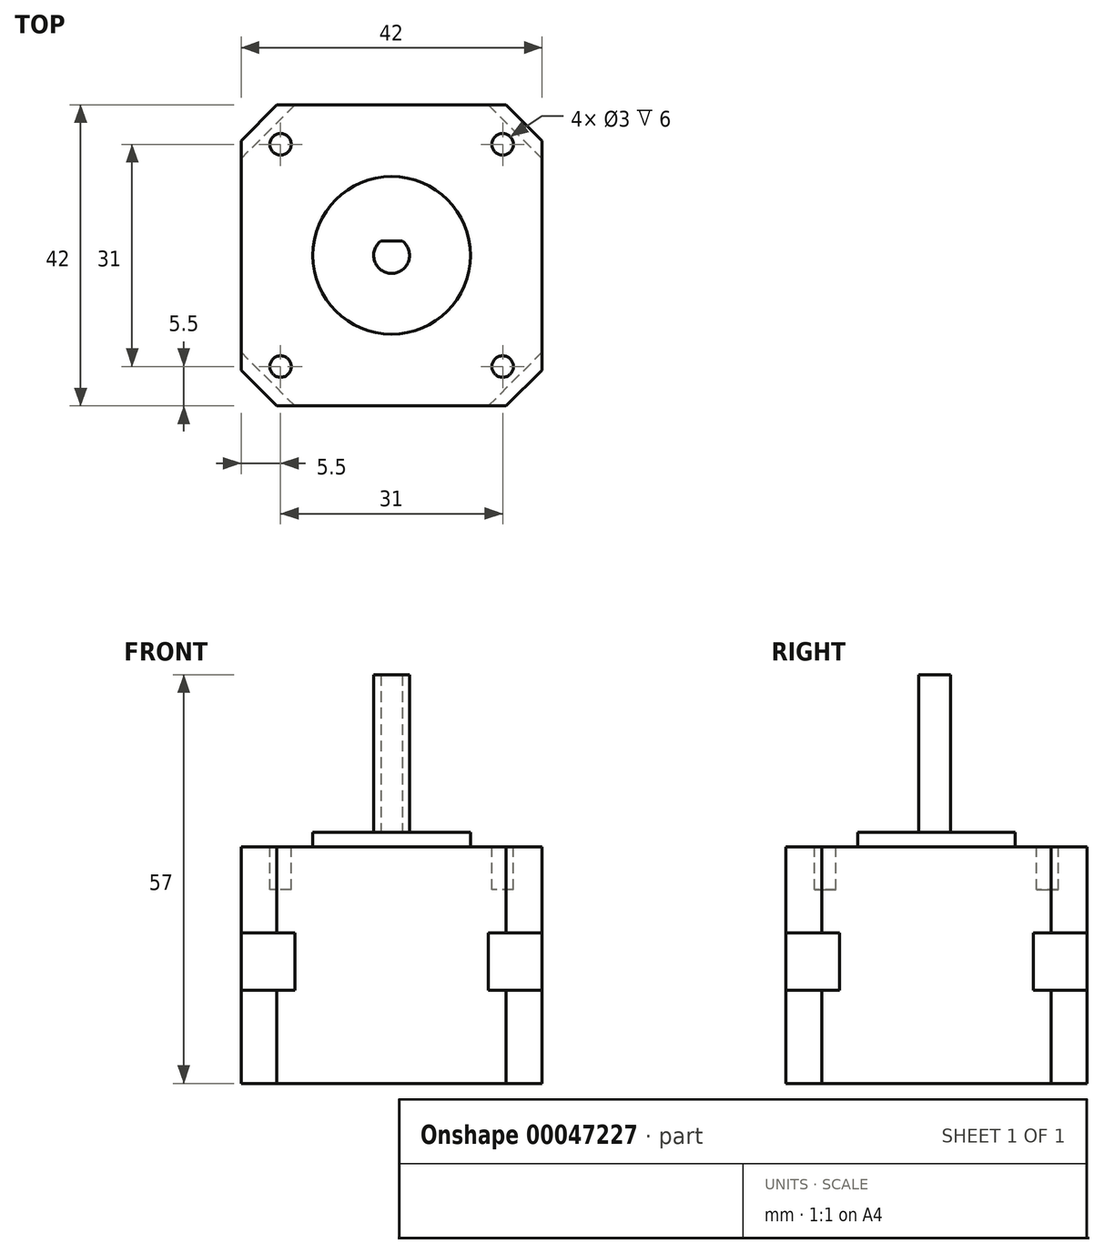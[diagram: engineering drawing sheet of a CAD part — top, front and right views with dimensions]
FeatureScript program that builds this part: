
annotation { "Feature Type Name" : "Feature", "Feature Type Description" : "" }
export const myFeature = defineFeature(function(context is Context, id is Id, definition is map)
    precondition{}
    {
        {
            var Q0;
            Q0=qCreatedBy(makeId("Top.planeOp"),FACE);
            var sketch = newSketch(context, id + "F0", { "sketchPlane" : qUnion([Q0])});
            skLineSegment(sketch, "E0.bottom", {"start": v(-21, 21) * mm, "end": v(21, 21) * mm});
            skLineSegment(sketch, "E0.top", {"start": v(-21, -21) * mm, "end": v(21, -21) * mm});
            skLineSegment(sketch, "E0.left", {"start": v(-21, 21) * mm, "end": v(-21, -21) * mm});
            skLineSegment(sketch, "E0.right", {"start": v(21, 21) * mm, "end": v(21, -21) * mm});
            skSolve(sketch);
        }
        {
            var Q0;
            Q0=makeQuery(id+"F0.imprint","IMPRINT",FACE,{"disambiguationData":[TD([[makeQuery(id+"F0.imprint","IMPRINT",EDGE,{"derivedFrom":sQuery(id+"F0.wireOp",EDGE,"E0.bottom")}),-1.0]])]});
            extrude(context, id + "F1", {"entities" : qUnion([Q0]), "endBound" : BoundingType.SYMMETRIC, "depth" : 8 * mm});
        }
        {
            var Q0;
            Q0=makeQuery(id+"F1.opExtrude","SWEPT_EDGE",EDGE,{"disambiguationData":[OSD([sQuery(id+"F0.wireOp",EDGE,"E0.bottom"),sQuery(id+"F0.wireOp",EDGE,"E0.right")])]});
            var Q1;
            Q1=makeQuery(id+"F1.opExtrude","SWEPT_EDGE",EDGE,{"disambiguationData":[OSD([sQuery(id+"F0.wireOp",EDGE,"E0.bottom"),sQuery(id+"F0.wireOp",EDGE,"E0.left")])]});
            var Q2;
            Q2=makeQuery(id+"F1.opExtrude","SWEPT_EDGE",EDGE,{"disambiguationData":[OSD([sQuery(id+"F0.wireOp",EDGE,"E0.top"),sQuery(id+"F0.wireOp",EDGE,"E0.left")])]});
            var Q3;
            Q3=makeQuery(id+"F1.opExtrude","SWEPT_EDGE",EDGE,{"disambiguationData":[OSD([sQuery(id+"F0.wireOp",EDGE,"E0.top"),sQuery(id+"F0.wireOp",EDGE,"E0.right")])]});
            chamfer(context, id + "F2", {"entities" : qUnion([Q0, Q1, Q2, Q3]), "width" : 7.5 * mm, "tangentPropagation" : true});
        }
        {
            var Q0;
            Q0=makeQuery(id+"F1.opExtrude","CAP_FACE",FACE,{"disambiguationData":[OSD([sQuery(id+"F0.wireOp",EDGE,"E0.bottom"),sQuery(id+"F0.wireOp",EDGE,"E0.top"),sQuery(id+"F0.wireOp",EDGE,"E0.left"),sQuery(id+"F0.wireOp",EDGE,"E0.right")])],"isStart":false});
            var sketch = newSketch(context, id + "F3", { "sketchPlane" : qUnion([Q0])});
            skLineSegment(sketch, "E1.0", {"start": v(-21, 21) * mm, "end": v(21, 21) * mm});
            skLineSegment(sketch, "E1.1", {"start": v(-21, 21) * mm, "end": v(-21, -21) * mm});
            skLineSegment(sketch, "E1.2", {"start": v(-21, -21) * mm, "end": v(21, -21) * mm});
            skLineSegment(sketch, "E1.3", {"start": v(21, 21) * mm, "end": v(21, -21) * mm});
            skSolve(sketch);
        }
        {
            var Q0;
            {var subQ0=sQuery(id+"F0.wireOp",EDGE,"E0.top");var subQ1=sQuery(id+"F0.wireOp",EDGE,"E0.right");var subQ2=sQuery(id+"F0.wireOp",EDGE,"E0.bottom");var subQ3=sQuery(id+"F0.wireOp",EDGE,"E0.left");var subQ4=makeQuery(id+"F1.opExtrude","CAP_FACE",FACE,{"disambiguationData":[OSD([subQ2,subQ0,subQ3,subQ1])],"isStart":false});var subQ8=makeQuery(id+"F2.opChamfer","BLEND_EDGE",EDGE,{"blendedFrom":[makeQuery(id+"F1.opExtrude","SWEPT_EDGE",EDGE,{"disambiguationData":[OSD([subQ2,subQ3])]}),subQ4],"blendedInto":[subQ4]});Q0=makeQuery(id+"F3.imprint","IMPRINT",FACE,{"disambiguationData":[TD([[makeQuery(id+"F3.imprint","IMPRINT",EDGE,{"derivedFrom":subQ8}),1.0]])]});}
            var Q1;
            {var subQ0=sQuery(id+"F0.wireOp",EDGE,"E0.bottom");var subQ1=sQuery(id+"F0.wireOp",EDGE,"E0.right");var subQ2=makeQuery(id+"F2.opChamfer","BLEND_EDGE",EDGE,{"blendedFrom":[makeQuery(id+"F1.opExtrude","SWEPT_EDGE",EDGE,{"disambiguationData":[OSD([subQ0,subQ1])]}),makeQuery(id+"F1.opExtrude","CAP_FACE",FACE,{"disambiguationData":[OSD([subQ0,sQuery(id+"F0.wireOp",EDGE,"E0.top"),sQuery(id+"F0.wireOp",EDGE,"E0.left"),subQ1])],"isStart":false})],"blendedInto":[makeQuery(id+"F1.opExtrude","CAP_FACE",FACE,{"disambiguationData":[OSD([subQ0,sQuery(id+"F0.wireOp",EDGE,"E0.top"),sQuery(id+"F0.wireOp",EDGE,"E0.left"),subQ1])],"isStart":false})]});Q1=makeQuery(id+"F3.imprint","IMPRINT",FACE,{"disambiguationData":[TD([[makeQuery(id+"F3.imprint","IMPRINT",EDGE,{"derivedFrom":subQ2}),-1.0]])]});}
            var Q2;
            {var subQ0=sQuery(id+"F0.wireOp",EDGE,"E0.bottom");var subQ1=sQuery(id+"F0.wireOp",EDGE,"E0.left");var subQ2=makeQuery(id+"F2.opChamfer","BLEND_EDGE",EDGE,{"blendedFrom":[makeQuery(id+"F1.opExtrude","SWEPT_EDGE",EDGE,{"disambiguationData":[OSD([subQ0,subQ1])]}),makeQuery(id+"F1.opExtrude","CAP_FACE",FACE,{"disambiguationData":[OSD([subQ0,sQuery(id+"F0.wireOp",EDGE,"E0.top"),subQ1,sQuery(id+"F0.wireOp",EDGE,"E0.right")])],"isStart":false})],"blendedInto":[makeQuery(id+"F1.opExtrude","CAP_FACE",FACE,{"disambiguationData":[OSD([subQ0,sQuery(id+"F0.wireOp",EDGE,"E0.top"),subQ1,sQuery(id+"F0.wireOp",EDGE,"E0.right")])],"isStart":false})]});Q2=makeQuery(id+"F3.imprint","IMPRINT",FACE,{"disambiguationData":[TD([[makeQuery(id+"F3.imprint","IMPRINT",EDGE,{"derivedFrom":subQ2}),-1.0]])]});}
            var Q3;
            {var subQ0=sQuery(id+"F0.wireOp",EDGE,"E0.top");var subQ1=sQuery(id+"F0.wireOp",EDGE,"E0.left");var subQ2=makeQuery(id+"F2.opChamfer","BLEND_EDGE",EDGE,{"blendedFrom":[makeQuery(id+"F1.opExtrude","SWEPT_EDGE",EDGE,{"disambiguationData":[OSD([subQ0,subQ1])]}),makeQuery(id+"F1.opExtrude","CAP_FACE",FACE,{"disambiguationData":[OSD([sQuery(id+"F0.wireOp",EDGE,"E0.bottom"),subQ0,subQ1,sQuery(id+"F0.wireOp",EDGE,"E0.right")])],"isStart":false})],"blendedInto":[makeQuery(id+"F1.opExtrude","CAP_FACE",FACE,{"disambiguationData":[OSD([sQuery(id+"F0.wireOp",EDGE,"E0.bottom"),subQ0,subQ1,sQuery(id+"F0.wireOp",EDGE,"E0.right")])],"isStart":false})]});Q3=makeQuery(id+"F3.imprint","IMPRINT",FACE,{"disambiguationData":[TD([[makeQuery(id+"F3.imprint","IMPRINT",EDGE,{"derivedFrom":subQ2}),-1.0]])]});}
            var Q4;
            {var subQ0=sQuery(id+"F0.wireOp",EDGE,"E0.top");var subQ1=sQuery(id+"F0.wireOp",EDGE,"E0.right");var subQ2=makeQuery(id+"F2.opChamfer","BLEND_EDGE",EDGE,{"blendedFrom":[makeQuery(id+"F1.opExtrude","SWEPT_EDGE",EDGE,{"disambiguationData":[OSD([subQ0,subQ1])]}),makeQuery(id+"F1.opExtrude","CAP_FACE",FACE,{"disambiguationData":[OSD([sQuery(id+"F0.wireOp",EDGE,"E0.bottom"),subQ0,sQuery(id+"F0.wireOp",EDGE,"E0.left"),subQ1])],"isStart":false})],"blendedInto":[makeQuery(id+"F1.opExtrude","CAP_FACE",FACE,{"disambiguationData":[OSD([sQuery(id+"F0.wireOp",EDGE,"E0.bottom"),subQ0,sQuery(id+"F0.wireOp",EDGE,"E0.left"),subQ1])],"isStart":false})]});Q4=makeQuery(id+"F3.imprint","IMPRINT",FACE,{"disambiguationData":[TD([[makeQuery(id+"F3.imprint","IMPRINT",EDGE,{"derivedFrom":subQ2}),-1.0]])]});}
            extrude(context, id + "F4", {"entities" : qUnion([Q0, Q1, Q2, Q3, Q4]), "operationType" : NewBodyOperationType.ADD, "depth" : 12 * mm});
        }
        {
            var Q0;
            Q0=makeQuery(id+"F4.opExtrude","SWEPT_EDGE",EDGE,{"disambiguationData":[OSD([sQuery(id+"F3.wireOp",EDGE,"E1.2"),sQuery(id+"F3.wireOp",EDGE,"E1.3")])]});
            var Q1;
            Q1=makeQuery(id+"F4.opExtrude","SWEPT_EDGE",EDGE,{"disambiguationData":[OSD([sQuery(id+"F3.wireOp",EDGE,"E1.1"),sQuery(id+"F3.wireOp",EDGE,"E1.2")])]});
            var Q2;
            Q2=makeQuery(id+"F4.opExtrude","SWEPT_EDGE",EDGE,{"disambiguationData":[OSD([sQuery(id+"F3.wireOp",EDGE,"E1.0"),sQuery(id+"F3.wireOp",EDGE,"E1.1")])]});
            var Q3;
            Q3=makeQuery(id+"F4.opExtrude","SWEPT_EDGE",EDGE,{"disambiguationData":[OSD([sQuery(id+"F3.wireOp",EDGE,"E1.0"),sQuery(id+"F3.wireOp",EDGE,"E1.3")])]});
            chamfer(context, id + "F5", {"entities" : qUnion([Q0, Q1, Q2, Q3]), "width" : 5 * mm, "tangentPropagation" : true});
        }
        {
            var Q0;
            Q0=makeQuery(id+"F1.opExtrude","CAP_FACE",FACE,{"disambiguationData":[OSD([sQuery(id+"F0.wireOp",EDGE,"E0.bottom"),sQuery(id+"F0.wireOp",EDGE,"E0.top"),sQuery(id+"F0.wireOp",EDGE,"E0.left"),sQuery(id+"F0.wireOp",EDGE,"E0.right")])],"isStart":true});
            var sketch = newSketch(context, id + "F6", { "sketchPlane" : qUnion([Q0])});
            skLineSegment(sketch, "E2.0.0", {"start": v(21, 16) * mm, "end": v(21, -16) * mm});
            skLineSegment(sketch, "E2.0.1", {"start": v(21, -16) * mm, "end": v(16, -21) * mm});
            skLineSegment(sketch, "E2.0.2", {"start": v(16, -21) * mm, "end": v(-16, -21) * mm});
            skLineSegment(sketch, "E2.0.3", {"start": v(-16, -21) * mm, "end": v(-21, -16) * mm});
            skLineSegment(sketch, "E2.0.4", {"start": v(-21, -16) * mm, "end": v(-21, 16) * mm});
            skLineSegment(sketch, "E2.0.5", {"start": v(-21, 16) * mm, "end": v(-16, 21) * mm});
            skLineSegment(sketch, "E2.0.6", {"start": v(-16, 21) * mm, "end": v(16, 21) * mm});
            skLineSegment(sketch, "E2.0.7", {"start": v(16, 21) * mm, "end": v(21, 16) * mm});
            skSolve(sketch);
        }
        {
            var Q0;
            Q0=qSketchRegion(id+"F6",true);
            extrude(context, id + "F7", {"entities" : qUnion([Q0]), "operationType" : NewBodyOperationType.ADD, "depth" : 13 * mm});
        }
        {
            var Q0;
            Q0=makeQuery(id+"F4.opExtrude","CAP_FACE",FACE,{"disambiguationData":[OSD([sQuery(id+"F3.wireOp",EDGE,"E1.0"),sQuery(id+"F3.wireOp",EDGE,"E1.1"),sQuery(id+"F3.wireOp",EDGE,"E1.2"),sQuery(id+"F3.wireOp",EDGE,"E1.3")])],"isStart":false});
            var sketch = newSketch(context, id + "F8", { "sketchPlane" : qUnion([Q0])});
            skCircle(sketch, "E3", {"center": v(0, 0) * mm, "radius": 11 * mm});
            skSolve(sketch);
        }
        {
            var Q0;
            Q0=qSketchRegion(id+"F8",true);
            extrude(context, id + "F9", {"entities" : qUnion([Q0]), "operationType" : NewBodyOperationType.ADD, "depth" : 2 * mm});
        }
        {
            var Q0;
            Q0=makeQuery(id+"F9.opExtrude","CAP_FACE",FACE,{"disambiguationData":[OSD([sQuery(id+"F8.wireOp",EDGE,"E3")])],"isStart":false});
            var sketch = newSketch(context, id + "F10", { "sketchPlane" : qUnion([Q0])});
            skCircle(sketch, "E4", {"center": v(0, 0) * mm, "radius": 2.5 * mm});
            skSolve(sketch);
        }
        {
            var Q0;
            Q0=makeQuery(id+"F10.imprint","IMPRINT",FACE,{"disambiguationData":[TD([[makeQuery(id+"F10.imprint","IMPRINT",EDGE,{"derivedFrom":sQuery(id+"F10.wireOp",EDGE,"E4")}),1.0]])]});
            extrude(context, id + "F11", {"entities" : qUnion([Q0]), "operationType" : NewBodyOperationType.ADD, "depth" : 22 * mm});
        }
        {
            var Q0;
            Q0=makeQuery(id+"F11.opExtrude","CAP_FACE",FACE,{"disambiguationData":[OSD([sQuery(id+"F10.wireOp",EDGE,"E4")])],"isStart":false});
            var sketch = newSketch(context, id + "F12", { "sketchPlane" : qUnion([Q0])});
            skLineSegment(sketch, "E5.bottom", {"start": v(-2.63, 2.93) * mm, "end": v(2.62, 2.93) * mm});
            skLineSegment(sketch, "E5.top", {"start": v(-2.63, 2) * mm, "end": v(2.62, 2) * mm});
            skLineSegment(sketch, "E5.left", {"start": v(-2.63, 2.93) * mm, "end": v(-2.63, 2) * mm});
            skLineSegment(sketch, "E5.right", {"start": v(2.62, 2.93) * mm, "end": v(2.62, 2) * mm});
            skSolve(sketch);
        }
        {
            var Q0;
            Q0=qSketchRegion(id+"F12",true);
            extrude(context, id + "F13", {"entities" : qUnion([Q0]), "operationType" : NewBodyOperationType.REMOVE, "oppositeDirection" : true, "depth" : 22 * mm});
        }
        {
            var Q0;
            Q0=makeQuery(id+"F4.opExtrude","CAP_FACE",FACE,{"disambiguationData":[OSD([sQuery(id+"F3.wireOp",EDGE,"E1.0"),sQuery(id+"F3.wireOp",EDGE,"E1.1"),sQuery(id+"F3.wireOp",EDGE,"E1.2"),sQuery(id+"F3.wireOp",EDGE,"E1.3")])],"isStart":false});
            var sketch = newSketch(context, id + "F14", { "sketchPlane" : qUnion([Q0])});
            skCircle(sketch, "E6", {"center": v(-15.5, 15.5) * mm, "radius": 1.5 * mm});
            skCircle(sketch, "E7.MirrorC", {"center": v(15.5, 15.5) * mm, "radius": 1.5 * mm});
            skCircle(sketch, "E8.MirrorC", {"center": v(-15.5, -15.5) * mm, "radius": 1.5 * mm});
            skCircle(sketch, "E9.MirrorC", {"center": v(15.5, -15.5) * mm, "radius": 1.5 * mm});
            skSolve(sketch);
        }
        {
            var Q0;
            Q0=qSketchRegion(id+"F14",true);
            extrude(context, id + "F15", {"entities" : qUnion([Q0]), "operationType" : NewBodyOperationType.REMOVE, "oppositeDirection" : true, "depth" : 6 * mm});
        }
    });
